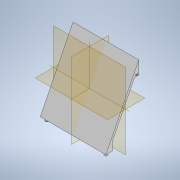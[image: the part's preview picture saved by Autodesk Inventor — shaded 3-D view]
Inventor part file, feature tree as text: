
AUTODESK INVENTOR PART (.ipt)
format: ipt  version: 2022.4 (Build 264492010, 492A)  size: 158,208 bytes
history: native  units: mm
features: revolve x4, sketch x3, extrude x2
ambient origin geometry x8: Origin, YZ Plane, XZ Plane, XY Plane, X Axis, Y Axis, Z Axis, Center Point
bodies: Solid1 (feature_tree)
feature tree (9):
  extrude  "Extrusion1"  Depth=100.0mm
  sketch  "Sketch4"  dims[d2=3.0mm d3=100.0mm d4=0.0mm]
  revolve  "Revolution2"  [1 undecoded]
  revolve  "Revolution3"  [1 undecoded]
  revolve  "Revolution4"  [1 undecoded]
  revolve  "Revolution5"  [1 undecoded]
  extrude  "Extrusion3"  Depth=5.0mm
  sketch  "Sketch1"  dims[d0=50.0mm d1=100.0mm]
  sketch  "Sketch5"  dims[d5=10.0mm d6=20.0mm d45=3.0mm d46=5.0mm d47=5.0mm d48=3.0mm d56=360.0deg d57=360.0deg d58=360.0deg d59=360.0deg d76=5.0mm d77=5.0mm d93=5.0mm d94=0.0mm d95=3.0mm d96=1.6mm d97=1.6mm d98=1.6mm d99=1.6mm d107=3.0mm d108=5.0mm d109=30.0mm d110=3.0mm d118=20.0mm d120=60.0mm d121=10.0mm d123=10.0mm d125=20.0mm d127=60.0mm d128=10.0mm d130=10.0mm]
note: 4 required parameter values undecoded (feature->parameter linkage not recoverable at this tier; creation-order binding heuristic only, values carry confidence <= 0.55)
